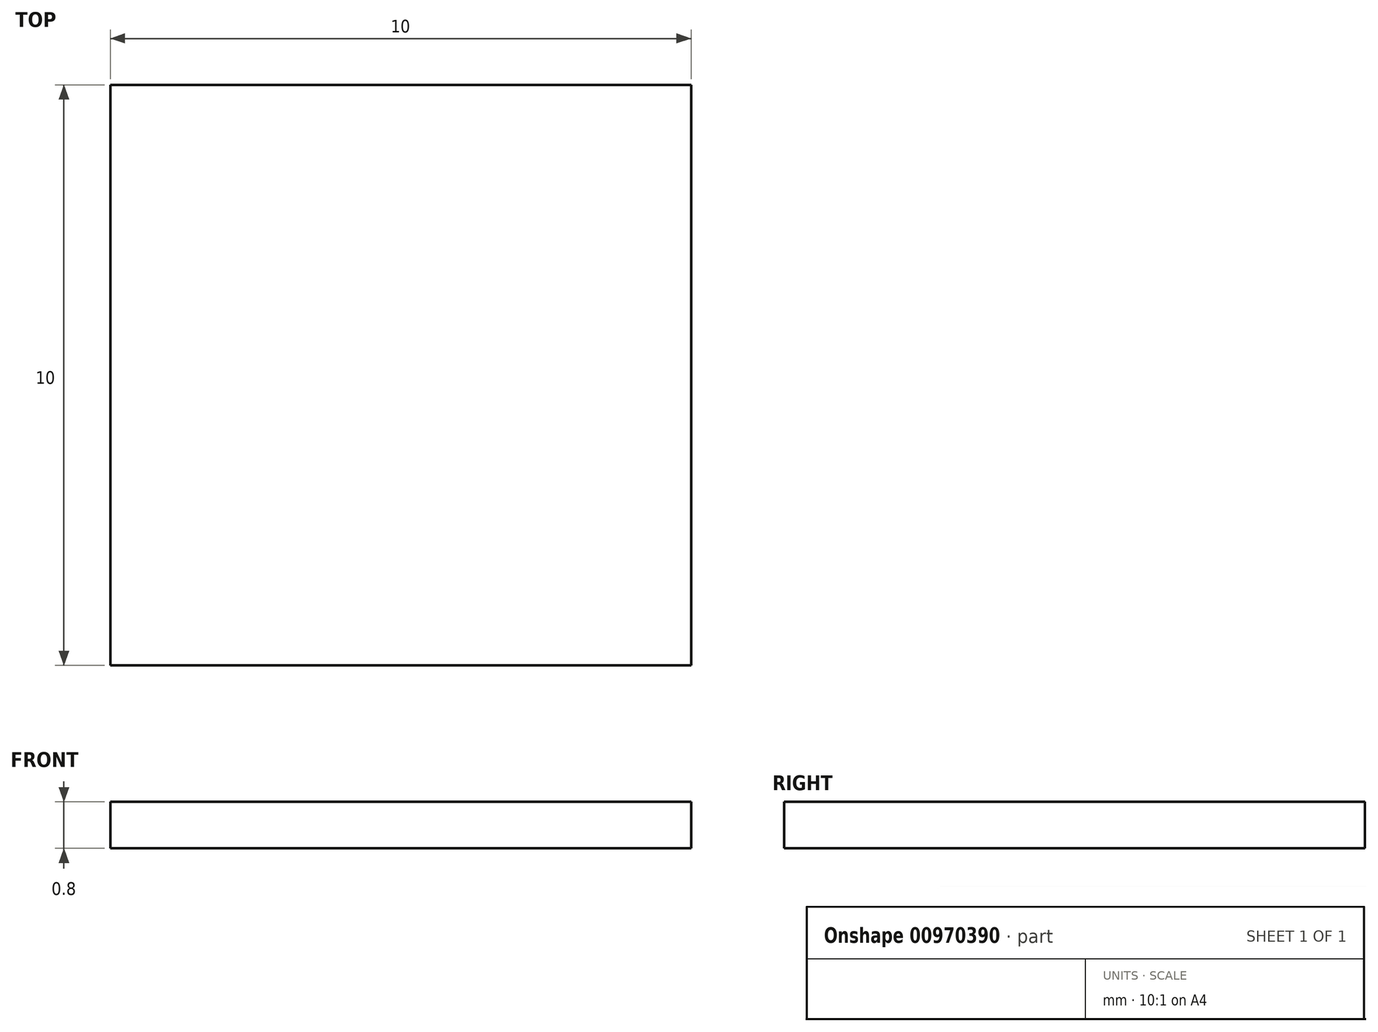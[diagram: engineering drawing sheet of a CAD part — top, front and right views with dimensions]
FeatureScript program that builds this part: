
annotation { "Feature Type Name" : "Feature", "Feature Type Description" : "" }
export const myFeature = defineFeature(function(context is Context, id is Id, definition is map)
    precondition{}
    {
        {
            var Q0;
            Q0=qCreatedBy(makeId("Top.planeOp"),FACE);
            var sketch = newSketch(context, id + "F0", { "sketchPlane" : qUnion([Q0])});
            skLineSegment(sketch, "E0.bottom", {"start": v(5, -5) * mm, "end": v(-5, -5) * mm});
            skLineSegment(sketch, "E0.top", {"start": v(5, 5) * mm, "end": v(-5, 5) * mm});
            skLineSegment(sketch, "E0.left", {"start": v(5, -5) * mm, "end": v(5, 5) * mm});
            skLineSegment(sketch, "E0.right", {"start": v(-5, -5) * mm, "end": v(-5, 5) * mm});
            skPoint(sketch, "E0.middle", {"position": v(0, 0) * mm});
            skSolve(sketch);
        }
        {
            var Q0;
            Q0=makeQuery(id+"F0.imprint","IMPRINT",FACE,{"disambiguationData":[TD([[makeQuery(id+"F0.imprint","IMPRINT",EDGE,{"derivedFrom":sQuery(id+"F0.wireOp",EDGE,"E0.bottom")}),-1.0]])]});
            extrude(context, id + "F1", {"entities" : qUnion([Q0]), "depth" : 0.8 * mm, "offsetDistance" : 25 * mm});
        }
    });
